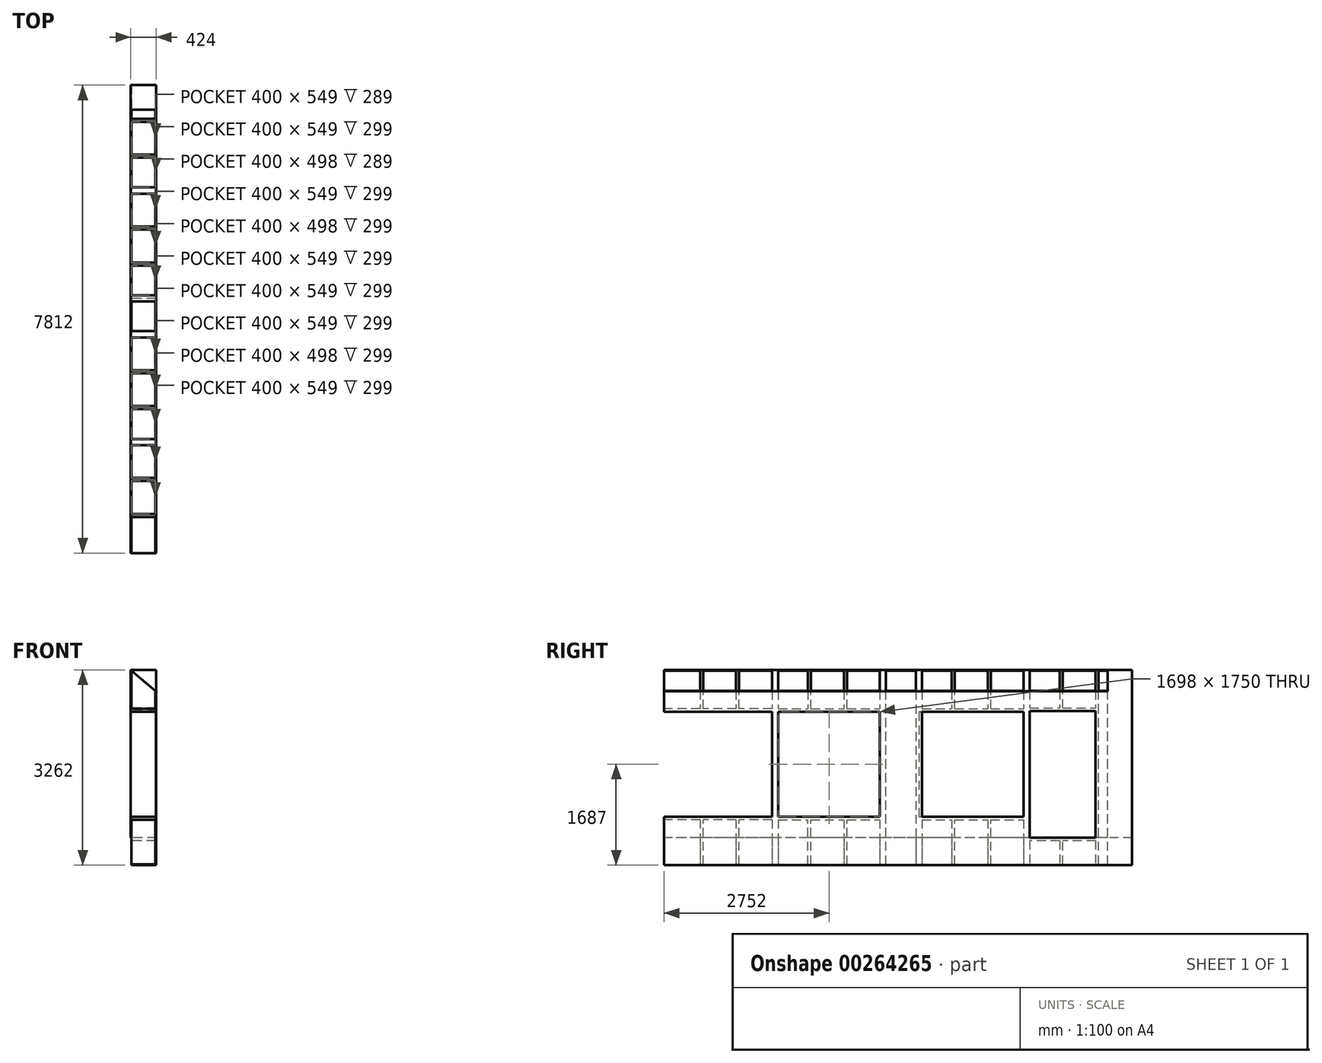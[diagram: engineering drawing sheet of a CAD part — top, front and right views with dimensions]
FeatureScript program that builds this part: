
annotation { "Feature Type Name" : "Feature", "Feature Type Description" : "" }
export const myFeature = defineFeature(function(context is Context, id is Id, definition is map)
    precondition{}
    {
        {
            var Q0;
            Q0=qCreatedBy(makeId("Right.planeOp"),FACE);
            var sketch = newSketch(context, id + "F0", { "sketchPlane" : qUnion([Q0])});
            skLineSegment(sketch, "E0.bottom", {"start": v(0, 0) * mm, "end": v(7400, 0) * mm});
            skLineSegment(sketch, "E0.top", {"start": v(0, 3250) * mm, "end": v(7400, 3250) * mm});
            skLineSegment(sketch, "E0.left", {"start": v(0, 0) * mm, "end": v(0, 3250) * mm});
            skLineSegment(sketch, "E0.right", {"start": v(7400, 0) * mm, "end": v(7400, 3250) * mm});
            skLineSegment(sketch, "E1", {"start": v(601, 3250) * mm, "end": v(601, 2601) * mm});
            skLineSegment(sketch, "E2", {"start": v(652, 0) * mm, "end": v(652, 749) * mm});
            skLineSegment(sketch, "E3.1.0.0", {"start": v(1252, 0) * mm, "end": v(1252, 749) * mm});
            skLineSegment(sketch, "E3.1.0.1", {"start": v(1201, 3250) * mm, "end": v(1201, 2601) * mm});
            skLineSegment(sketch, "E3.2.0.1", {"start": v(1801, 3250) * mm, "end": v(1801, 749) * mm});
            skLineSegment(sketch, "E3.4.0.0", {"start": v(3052, 0) * mm, "end": v(3052, 749) * mm});
            skLineSegment(sketch, "E3.4.0.1", {"start": v(3001, 3250) * mm, "end": v(3001, 2601) * mm});
            skLineSegment(sketch, "E3.5.0.1", {"start": v(3601, 3250) * mm, "end": v(3601, 0) * mm});
            skLineSegment(sketch, "E3.6.0.0", {"start": v(4252, 0) * mm, "end": v(4252, 3250) * mm});
            skLineSegment(sketch, "E3.6.0.1", {"start": v(4201, 3250) * mm, "end": v(4201, 0) * mm});
            skLineSegment(sketch, "E3.7.0.0", {"start": v(4852, 0) * mm, "end": v(4852, 749) * mm});
            skLineSegment(sketch, "E3.7.0.1", {"start": v(4801, 3250) * mm, "end": v(4801, 2601) * mm});
            skLineSegment(sketch, "E3.8.0.0", {"start": v(5452, 0) * mm, "end": v(5452, 749) * mm});
            skLineSegment(sketch, "E3.8.0.1", {"start": v(5401, 3250) * mm, "end": v(5401, 2601) * mm});
            skLineSegment(sketch, "E3.9.0.0", {"start": v(6052, 0) * mm, "end": v(6052, 749) * mm});
            skLineSegment(sketch, "E3.9.0.1", {"start": v(6001, 3250) * mm, "end": v(6001, 2601) * mm});
            skLineSegment(sketch, "E3.10.0.0", {"start": v(6652, 0) * mm, "end": v(6652, 399) * mm});
            skLineSegment(sketch, "E3.10.0.1", {"start": v(6601, 3250) * mm, "end": v(6601, 2611) * mm});
            skLineSegment(sketch, "E3.11.0.0", {"start": v(7252, 0) * mm, "end": v(7252, 3250) * mm});
            skLineSegment(sketch, "E3.11.0.1", {"start": v(7201, 3250) * mm, "end": v(7201, 0) * mm});
            skLineSegment(sketch, "E3.direction1", {"start": v(652, 0) * mm, "end": v(1252, 0) * mm, "construction": true});
            skLineSegment(sketch, "E4.bottom", {"start": v(7400, 0) * mm, "end": v(7812, 0) * mm});
            skLineSegment(sketch, "E4.top", {"start": v(7400, 3250) * mm, "end": v(7812, 3250) * mm});
            skLineSegment(sketch, "E4.right", {"start": v(7812, 0) * mm, "end": v(7812, 3250) * mm});
            skLineSegment(sketch, "E5", {"start": v(6001, 2550) * mm, "end": v(4252, 2550) * mm});
            skLineSegment(sketch, "E6", {"start": v(4252, 2550) * mm, "end": v(4252, 800) * mm});
            skLineSegment(sketch, "E7", {"start": v(4252, 800) * mm, "end": v(6001, 800) * mm});
            skLineSegment(sketch, "E8", {"start": v(4252, 2601) * mm, "end": v(6001, 2601) * mm});
            skLineSegment(sketch, "E9", {"start": v(4252, 749) * mm, "end": v(6001, 749) * mm});
            skLineSegment(sketch, "E10.trimOffspring", {"start": v(6001, 749) * mm, "end": v(6001, 0) * mm});
            skLineSegment(sketch, "E11.trimOffspring", {"start": v(6052, 2601) * mm, "end": v(6052, 3250) * mm});
            skLineSegment(sketch, "E12.trimOffspring", {"start": v(6601, 399) * mm, "end": v(6601, 0) * mm});
            skLineSegment(sketch, "E13.trimOffspring", {"start": v(6652, 2611) * mm, "end": v(6652, 3250) * mm});
            skLineSegment(sketch, "E14", {"start": v(0, 2550) * mm, "end": v(1801, 2550) * mm});
            skLineSegment(sketch, "E15", {"start": v(1801, 2601) * mm, "end": v(0, 2601) * mm});
            skLineSegment(sketch, "E16", {"start": v(1801, 749) * mm, "end": v(0, 749) * mm});
            skLineSegment(sketch, "E17", {"start": v(1801, 800) * mm, "end": v(0, 800) * mm});
            skLineSegment(sketch, "E18.trimOffspring", {"start": v(1201, 749) * mm, "end": v(1201, 0) * mm});
            skLineSegment(sketch, "E19.trimOffspring", {"start": v(1252, 2601) * mm, "end": v(1252, 3250) * mm});
            skLineSegment(sketch, "E20.trimOffspring", {"start": v(1801, 749) * mm, "end": v(1801, 0) * mm});
            skLineSegment(sketch, "E21.trimOffspring", {"start": v(3001, 749) * mm, "end": v(3001, 0) * mm});
            skLineSegment(sketch, "E22.trimOffspring", {"start": v(3052, 2601) * mm, "end": v(3052, 3250) * mm});
            skPoint(sketch, "E23.orphan", {"position": v(2401, 3250) * mm});
            skPoint(sketch, "E24.orphan", {"position": v(2401, 0) * mm});
            skLineSegment(sketch, "E25.trimOffspring", {"start": v(601, 749) * mm, "end": v(601, 0) * mm});
            skLineSegment(sketch, "E26.trimOffspring", {"start": v(652, 2601) * mm, "end": v(652, 3250) * mm});
            skLineSegment(sketch, "E27", {"start": v(1852, 3250) * mm, "end": v(1852, 0) * mm});
            skLineSegment(sketch, "E28", {"start": v(1903, 3250) * mm, "end": v(1903, 0) * mm});
            skLineSegment(sketch, "E29", {"start": v(1903, 2601) * mm, "end": v(3601, 2601) * mm});
            skLineSegment(sketch, "E30", {"start": v(1903, 2550) * mm, "end": v(3601, 2550) * mm});
            skLineSegment(sketch, "E31", {"start": v(3652, 3250) * mm, "end": v(3652, 0) * mm});
            skLineSegment(sketch, "E32", {"start": v(1903, 800) * mm, "end": v(3601, 800) * mm});
            skLineSegment(sketch, "E33", {"start": v(1903, 749) * mm, "end": v(3601, 749) * mm});
            skLineSegment(sketch, "E34", {"start": v(2401, 3250) * mm, "end": v(2401, 2601) * mm});
            skLineSegment(sketch, "E35", {"start": v(2401, 0) * mm, "end": v(2401, 749) * mm});
            skLineSegment(sketch, "E36", {"start": v(2452, 0) * mm, "end": v(2452, 749) * mm});
            skLineSegment(sketch, "E37", {"start": v(2452, 2601) * mm, "end": v(2452, 3250) * mm});
            skLineSegment(sketch, "E38", {"start": v(6052, 2601) * mm, "end": v(6052, 749) * mm});
            skLineSegment(sketch, "E39", {"start": v(6001, 2601) * mm, "end": v(6001, 749) * mm});
            skLineSegment(sketch, "E40", {"start": v(6103, 450) * mm, "end": v(7201, 450) * mm});
            skLineSegment(sketch, "E41", {"start": v(7201, 399) * mm, "end": v(6103, 399) * mm});
            skLineSegment(sketch, "E42", {"start": v(6103, 2560) * mm, "end": v(7201, 2560) * mm});
            skLineSegment(sketch, "E43", {"start": v(6103, 2611) * mm, "end": v(7201, 2611) * mm});
            skLineSegment(sketch, "E44", {"start": v(6103, 3250) * mm, "end": v(6103, 0) * mm});
            skLineSegment(sketch, "E45.trimOffspring", {"start": v(4801, 749) * mm, "end": v(4801, 0) * mm});
            skLineSegment(sketch, "E46.trimOffspring", {"start": v(4852, 2601) * mm, "end": v(4852, 3250) * mm});
            skLineSegment(sketch, "E47.trimOffspring", {"start": v(5401, 749) * mm, "end": v(5401, 0) * mm});
            skLineSegment(sketch, "E48.trimOffspring", {"start": v(5452, 2601) * mm, "end": v(5452, 3250) * mm});
            skPoint(sketch, "E49.orphan", {"position": v(6601, 2560) * mm});
            skPoint(sketch, "E50.orphan", {"position": v(6652, 2560) * mm});
            skPoint(sketch, "E51.orphan", {"position": v(6601, 450) * mm});
            skPoint(sketch, "E52.orphan", {"position": v(6652, 450) * mm});
            skLineSegment(sketch, "E53", {"start": v(4303, 3250) * mm, "end": v(4303, 0) * mm});
            skLineSegment(sketch, "E54", {"start": v(3703, 0) * mm, "end": v(3703, 3250) * mm});
            skSolve(sketch);
        }
        {
            var Q0;
            {var subQ0=sQuery(id+"F0.wireOp",EDGE,"E1");Q0=makeQuery(id+"F0.imprint","IMPRINT",FACE,{"disambiguationData":[TD([[makeQuery(id+"F0.imprint","IMPRINT",EDGE,{"derivedFrom":subQ0}),1.0]])]});}
            var Q1;
            {var subQ0=sQuery(id+"F0.wireOp",EDGE,"E3.7.0.0");Q1=makeQuery(id+"F0.imprint","IMPRINT",FACE,{"disambiguationData":[TD([[makeQuery(id+"F0.imprint","IMPRINT",EDGE,{"derivedFrom":subQ0}),1.0]])]});}
            var Q2;
            {var subQ0=sQuery(id+"F0.wireOp",EDGE,"E3.1.0.0");Q2=makeQuery(id+"F0.imprint","IMPRINT",FACE,{"disambiguationData":[TD([[makeQuery(id+"F0.imprint","IMPRINT",EDGE,{"derivedFrom":subQ0}),1.0]])]});}
            var Q3;
            {var subQ0=sQuery(id+"F0.wireOp",EDGE,"E3.2.0.0");Q3=makeQuery(id+"F0.imprint","IMPRINT",FACE,{"disambiguationData":[TD([[makeQuery(id+"F0.imprint","IMPRINT",EDGE,{"derivedFrom":subQ0}),1.0]])]});}
            var Q4;
            {var subQ0=sQuery(id+"F0.wireOp",EDGE,"E3.4.0.0");Q4=makeQuery(id+"F0.imprint","IMPRINT",FACE,{"disambiguationData":[TD([[makeQuery(id+"F0.imprint","IMPRINT",EDGE,{"derivedFrom":subQ0}),1.0]])]});}
            var Q5;
            {var subQ0=sQuery(id+"F0.wireOp",EDGE,"E3.5.0.0");Q5=makeQuery(id+"F0.imprint","IMPRINT",FACE,{"disambiguationData":[TD([[makeQuery(id+"F0.imprint","IMPRINT",EDGE,{"derivedFrom":subQ0}),1.0]])]});}
            var Q6;
            {var subQ0=sQuery(id+"F0.wireOp",EDGE,"E3.9.0.0");Q6=makeQuery(id+"F0.imprint","IMPRINT",FACE,{"disambiguationData":[TD([[makeQuery(id+"F0.imprint","IMPRINT",EDGE,{"derivedFrom":subQ0}),1.0]])]});}
            var Q7;
            {var subQ0=sQuery(id+"F0.wireOp",EDGE,"E3.10.0.0");Q7=makeQuery(id+"F0.imprint","IMPRINT",FACE,{"disambiguationData":[TD([[makeQuery(id+"F0.imprint","IMPRINT",EDGE,{"derivedFrom":subQ0}),1.0]])]});}
            var Q8;
            {var subQ0=sQuery(id+"F0.wireOp",EDGE,"E3.1.0.1");Q8=makeQuery(id+"F0.imprint","IMPRINT",FACE,{"disambiguationData":[TD([[makeQuery(id+"F0.imprint","IMPRINT",EDGE,{"derivedFrom":subQ0}),1.0]])]});}
            var Q9;
            {var subQ0=sQuery(id+"F0.wireOp",EDGE,"E3.2.0.1");Q9=makeQuery(id+"F0.imprint","IMPRINT",FACE,{"disambiguationData":[TD([[makeQuery(id+"F0.imprint","IMPRINT",EDGE,{"derivedFrom":subQ0}),1.0]])]});}
            var Q10;
            {var subQ0=sQuery(id+"F0.wireOp",EDGE,"E3.4.0.1");Q10=makeQuery(id+"F0.imprint","IMPRINT",FACE,{"disambiguationData":[TD([[makeQuery(id+"F0.imprint","IMPRINT",EDGE,{"derivedFrom":subQ0}),1.0]])]});}
            var Q11;
            {var subQ0=sQuery(id+"F0.wireOp",EDGE,"E3.5.0.1");Q11=makeQuery(id+"F0.imprint","IMPRINT",FACE,{"disambiguationData":[TD([[makeQuery(id+"F0.imprint","IMPRINT",EDGE,{"derivedFrom":subQ0}),1.0]])]});}
            var Q12;
            {var subQ0=sQuery(id+"F0.wireOp",EDGE,"E3.9.0.1");Q12=makeQuery(id+"F0.imprint","IMPRINT",FACE,{"disambiguationData":[TD([[makeQuery(id+"F0.imprint","IMPRINT",EDGE,{"derivedFrom":subQ0}),1.0]])]});}
            var Q13;
            {var subQ0=sQuery(id+"F0.wireOp",EDGE,"E3.10.0.1");Q13=makeQuery(id+"F0.imprint","IMPRINT",FACE,{"disambiguationData":[TD([[makeQuery(id+"F0.imprint","IMPRINT",EDGE,{"derivedFrom":subQ0}),1.0]])]});}
            var Q14;
            {var subQ4=sQuery(id+"F0.wireOp",EDGE,"E3.3.0.0");Q14=makeQuery(id+"F0.imprint","IMPRINT",FACE,{"disambiguationData":[TD([[makeQuery(id+"F0.imprint","IMPRINT",EDGE,{"derivedFrom":subQ4}),1.0]])]});}
            var Q15;
            {var subQ4=sQuery(id+"F0.wireOp",EDGE,"E3.3.0.0");Q15=makeQuery(id+"F0.imprint","IMPRINT",FACE,{"disambiguationData":[TD([[makeQuery(id+"F0.imprint","IMPRINT",EDGE,{"derivedFrom":subQ4}),-1.0]])]});}
            var Q16;
            {var subQ0=sQuery(id+"F0.wireOp",EDGE,"E3.6.0.0");Q16=makeQuery(id+"F0.imprint","IMPRINT",FACE,{"disambiguationData":[TD([[makeQuery(id+"F0.imprint","IMPRINT",EDGE,{"derivedFrom":subQ0}),1.0]])]});}
            var Q17;
            {var subQ5=sQuery(id+"F0.wireOp",EDGE,"E3.8.0.1");Q17=makeQuery(id+"F0.imprint","IMPRINT",FACE,{"disambiguationData":[TD([[makeQuery(id+"F0.imprint","IMPRINT",EDGE,{"derivedFrom":subQ5}),1.0]])]});}
            var Q18;
            {var subQ4=sQuery(id+"F0.wireOp",EDGE,"E3.11.0.0");Q18=makeQuery(id+"F0.imprint","IMPRINT",FACE,{"disambiguationData":[TD([[makeQuery(id+"F0.imprint","IMPRINT",EDGE,{"derivedFrom":subQ4}),1.0]])]});}
            var Q19;
            {var subQ6=sQuery(id+"F0.wireOp",EDGE,"E17");Q19=makeQuery(id+"F0.imprint","IMPRINT",FACE,{"disambiguationData":[TD([[makeQuery(id+"F0.imprint","IMPRINT",EDGE,{"derivedFrom":subQ6}),1.0]])]});}
            var Q20;
            {var subQ5=sQuery(id+"F0.wireOp",EDGE,"E14");Q20=makeQuery(id+"F0.imprint","IMPRINT",FACE,{"disambiguationData":[TD([[makeQuery(id+"F0.imprint","IMPRINT",EDGE,{"derivedFrom":subQ5}),1.0]])]});}
            var Q21;
            {var subQ5=sQuery(id+"F0.wireOp",EDGE,"g8gJmtVJ-kyqd-3TZ6-0mUu-25J443NQGefS");Q21=makeQuery(id+"F0.imprint","IMPRINT",FACE,{"disambiguationData":[TD([[makeQuery(id+"F0.imprint","IMPRINT",EDGE,{"derivedFrom":subQ5}),1.0]])]});}
            var Q22;
            {var subQ4=sQuery(id+"F0.wireOp",EDGE,"8giRP16X-JChZ-mFzo-qgzl-EssFRHRw9BJs");Q22=makeQuery(id+"F0.imprint","IMPRINT",FACE,{"disambiguationData":[TD([[makeQuery(id+"F0.imprint","IMPRINT",EDGE,{"derivedFrom":subQ4}),-1.0]])]});}
            var Q23;
            Q23=makeQuery(id+"F0.imprint","IMPRINT",FACE,{"disambiguationData":[TD([[makeQuery(id+"F0.imprint","IMPRINT",EDGE,{"derivedFrom":sQuery(id+"F0.wireOp",EDGE,"E4.bottom")}),1.0]])]});
            var Q24;
            {var subQ4=sQuery(id+"F0.wireOp",EDGE,"E7");Q24=makeQuery(id+"F0.imprint","IMPRINT",FACE,{"disambiguationData":[TD([[makeQuery(id+"F0.imprint","IMPRINT",EDGE,{"derivedFrom":subQ4}),-1.0]])]});}
            var Q25;
            {var subQ0=sQuery(id+"F0.wireOp",EDGE,"E2");Q25=makeQuery(id+"F0.imprint","IMPRINT",FACE,{"disambiguationData":[TD([[makeQuery(id+"F0.imprint","IMPRINT",EDGE,{"derivedFrom":subQ0}),1.0]])]});}
            var Q26;
            {var subQ4=sQuery(id+"F0.wireOp",EDGE,"E27");Q26=makeQuery(id+"F0.imprint","IMPRINT",FACE,{"disambiguationData":[TD([[makeQuery(id+"F0.imprint","IMPRINT",EDGE,{"derivedFrom":subQ4}),1.0]])]});}
            var Q27;
            {var subQ0=sQuery(id+"F0.wireOp",EDGE,"E32");Q27=makeQuery(id+"F0.imprint","IMPRINT",FACE,{"disambiguationData":[TD([[makeQuery(id+"F0.imprint","IMPRINT",EDGE,{"derivedFrom":subQ0}),-1.0]])]});}
            var Q28;
            {var subQ0=sQuery(id+"F0.wireOp",EDGE,"E35");Q28=makeQuery(id+"F0.imprint","IMPRINT",FACE,{"disambiguationData":[TD([[makeQuery(id+"F0.imprint","IMPRINT",EDGE,{"derivedFrom":subQ0}),-1.0]])]});}
            var Q29;
            {var subQ0=sQuery(id+"F0.wireOp",EDGE,"E34");Q29=makeQuery(id+"F0.imprint","IMPRINT",FACE,{"disambiguationData":[TD([[makeQuery(id+"F0.imprint","IMPRINT",EDGE,{"derivedFrom":subQ0}),1.0]])]});}
            var Q30;
            {var subQ5=sQuery(id+"F0.wireOp",EDGE,"E30");Q30=makeQuery(id+"F0.imprint","IMPRINT",FACE,{"disambiguationData":[TD([[makeQuery(id+"F0.imprint","IMPRINT",EDGE,{"derivedFrom":subQ5}),1.0]])]});}
            var Q31;
            {var subQ3=sQuery(id+"F0.wireOp",EDGE,"E42");Q31=makeQuery(id+"F0.imprint","IMPRINT",FACE,{"disambiguationData":[TD([[makeQuery(id+"F0.imprint","IMPRINT",EDGE,{"derivedFrom":subQ3}),1.0]])]});}
            var Q32;
            {var subQ3=sQuery(id+"F0.wireOp",EDGE,"E40");Q32=makeQuery(id+"F0.imprint","IMPRINT",FACE,{"disambiguationData":[TD([[makeQuery(id+"F0.imprint","IMPRINT",EDGE,{"derivedFrom":subQ3}),-1.0]])]});}
            var Q33;
            {var subQ0=sQuery(id+"F0.wireOp",EDGE,"E3.8.0.0");Q33=makeQuery(id+"F0.imprint","IMPRINT",FACE,{"disambiguationData":[TD([[makeQuery(id+"F0.imprint","IMPRINT",EDGE,{"derivedFrom":subQ0}),1.0]])]});}
            var Q34;
            {var subQ0=sQuery(id+"F0.wireOp",EDGE,"E3.9.0.0");Q34=makeQuery(id+"F0.imprint","IMPRINT",FACE,{"disambiguationData":[TD([[makeQuery(id+"F0.imprint","IMPRINT",EDGE,{"derivedFrom":subQ0}),-1.0]])]});}
            var Q35;
            {var subQ0=sQuery(id+"F0.wireOp",EDGE,"E3.7.0.1");Q35=makeQuery(id+"F0.imprint","IMPRINT",FACE,{"disambiguationData":[TD([[makeQuery(id+"F0.imprint","IMPRINT",EDGE,{"derivedFrom":subQ0}),1.0]])]});}
            var Q36;
            {var subQ4=sQuery(id+"F0.wireOp",EDGE,"E5");var subQ8=sQuery(id+"F0.wireOp",EDGE,"E39");var subQ9=makeQuery(id+"F0.imprint","INTERSECT",VERTEX,{"derivedFrom":[subQ4,subQ8]});Q36=makeQuery(id+"F0.imprint","IMPRINT",FACE,{"disambiguationData":[TD([[makeQuery(id+"F0.imprint","IMPRINT",EDGE,{"disambiguationData":[TD([[subQ9,-1.0]])],"derivedFrom":subQ4}),-1.0]])]});}
            var Q37;
            {var subQ0=sQuery(id+"F0.wireOp",EDGE,"E3.6.0.0");var subQ1=sQuery(id+"F0.wireOp",EDGE,"E0.top");var subQ2=makeQuery(id+"F0.imprint","INTERSECT",VERTEX,{"derivedFrom":[subQ1,subQ0]});Q37=makeQuery(id+"F0.imprint","IMPRINT",FACE,{"disambiguationData":[TD([[makeQuery(id+"F0.imprint","IMPRINT",EDGE,{"disambiguationData":[TD([[subQ2,-1.0]])],"derivedFrom":subQ1}),-1.0]])]});}
            var Q38;
            {var subQ0=sQuery(id+"F0.wireOp",EDGE,"E6");Q38=makeQuery(id+"F0.imprint","IMPRINT",FACE,{"disambiguationData":[TD([[makeQuery(id+"F0.imprint","IMPRINT",EDGE,{"derivedFrom":subQ0}),1.0]])]});}
            var Q39;
            {var subQ1=sQuery(id+"F0.wireOp",EDGE,"E3.6.0.0");var subQ3=sQuery(id+"F0.wireOp",EDGE,"E8");var subQ4=makeQuery(id+"F0.imprint","INTERSECT",VERTEX,{"derivedFrom":[subQ1,subQ3]});Q39=makeQuery(id+"F0.imprint","IMPRINT",FACE,{"disambiguationData":[TD([[makeQuery(id+"F0.imprint","IMPRINT",EDGE,{"disambiguationData":[TD([[subQ4,-1.0]])],"derivedFrom":subQ3}),-1.0]])]});}
            var Q40;
            {var subQ6=sQuery(id+"F0.wireOp",EDGE,"E39");var subQ7=sQuery(id+"F0.wireOp",EDGE,"E7");var subQ8=makeQuery(id+"F0.imprint","INTERSECT",VERTEX,{"derivedFrom":[subQ7,subQ6]});Q40=makeQuery(id+"F0.imprint","IMPRINT",FACE,{"disambiguationData":[TD([[makeQuery(id+"F0.imprint","IMPRINT",EDGE,{"disambiguationData":[TD([[subQ8,1.0]])],"derivedFrom":subQ7}),-1.0]])]});}
            var Q41;
            {var subQ0=sQuery(id+"F0.wireOp",EDGE,"E3.6.0.0");var subQ1=sQuery(id+"F0.wireOp",EDGE,"E0.bottom");var subQ2=makeQuery(id+"F0.imprint","INTERSECT",VERTEX,{"derivedFrom":[subQ1,subQ0]});Q41=makeQuery(id+"F0.imprint","IMPRINT",FACE,{"disambiguationData":[TD([[makeQuery(id+"F0.imprint","IMPRINT",EDGE,{"disambiguationData":[TD([[subQ2,-1.0]])],"derivedFrom":subQ1}),1.0]])]});}
            var Q42;
            {var subQ0=sQuery(id+"F0.wireOp",EDGE,"E31");Q42=makeQuery(id+"F0.imprint","IMPRINT",FACE,{"disambiguationData":[TD([[makeQuery(id+"F0.imprint","IMPRINT",EDGE,{"derivedFrom":subQ0}),1.0]])]});}
            extrude(context, id + "F1", {"entities" : qUnion([Q0, Q1, Q2, Q3, Q4, Q5, Q6, Q7, Q8, Q9, Q10, Q11, Q12, Q13, Q14, Q15, Q16, Q17, Q18, Q19, Q20, Q21, Q22, Q23, Q24, Q25, Q26, Q27, Q28, Q29, Q30, Q31, Q32, Q33, Q34, Q35, Q36, Q37, Q38, Q39, Q40, Q41, Q42]), "depth" : 400 * mm, "offsetDistance" : 25 * mm});
        }
        {
            var Q0;
            Q0=makeQuery(id+"F1.opExtrude","CAP_FACE",FACE,{"disambiguationData":[OSD([sQuery(id+"F0.wireOp",EDGE,"E0.bottom"),sQuery(id+"F0.wireOp",EDGE,"E0.top"),sQuery(id+"F0.wireOp",EDGE,"E1"),sQuery(id+"F0.wireOp",EDGE,"E3.1.0.0"),sQuery(id+"F0.wireOp",EDGE,"E3.1.0.1"),sQuery(id+"F0.wireOp",EDGE,"E3.2.0.0"),sQuery(id+"F0.wireOp",EDGE,"E3.2.0.1"),sQuery(id+"F0.wireOp",EDGE,"E3.3.0.1"),sQuery(id+"F0.wireOp",EDGE,"E3.4.0.0"),sQuery(id+"F0.wireOp",EDGE,"E3.4.0.1"),sQuery(id+"F0.wireOp",EDGE,"E3.5.0.0"),sQuery(id+"F0.wireOp",EDGE,"E3.5.0.1"),sQuery(id+"F0.wireOp",EDGE,"E3.6.0.0"),sQuery(id+"F0.wireOp",EDGE,"E3.6.0.1"),sQuery(id+"F0.wireOp",EDGE,"E14"),sQuery(id+"F0.wireOp",EDGE,"E15"),sQuery(id+"F0.wireOp",EDGE,"E16"),sQuery(id+"F0.wireOp",EDGE,"E17"),sQuery(id+"F0.wireOp",EDGE,"E18.trimOffspring"),sQuery(id+"F0.wireOp",EDGE,"E19.trimOffspring"),sQuery(id+"F0.wireOp",EDGE,"E20.trimOffspring"),sQuery(id+"F0.wireOp",EDGE,"9c03632e-1589-4136-8b4a-7c2474c811de.trimOffspring"),sQuery(id+"F0.wireOp",EDGE,"q5mhnWq2-EtEE-7vjZ-CXv9-tcfamw4Ga4Gx"),sQuery(id+"F0.wireOp",EDGE,"FWBOiuXw-SkXY-gYsp-Law7-7kdNVkWK1UfF"),sQuery(id+"F0.wireOp",EDGE,"g8gJmtVJ-kyqd-3TZ6-0mUu-25J443NQGefS"),sQuery(id+"F0.wireOp",EDGE,"8giRP16X-JChZ-mFzo-qgzl-EssFRHRw9BJs"),sQuery(id+"F0.wireOp",EDGE,"Jl1Ox0xb-Z49W-AvNk-nDFi-4VLoJo9j3xGR"),sQuery(id+"F0.wireOp",EDGE,"E21.trimOffspring"),sQuery(id+"F0.wireOp",EDGE,"E22.trimOffspring"),sQuery(id+"F0.wireOp",EDGE,"a5652450-98d4-451b-b7c5-3669fa653a12.trimOffspring"),sQuery(id+"F0.wireOp",EDGE,"9c86828a-2c14-4f8d-8b37-fce8d1982b22.trimOffspring"),sQuery(id+"F0.wireOp",EDGE,"YK2BJbLm-Syb8-vEb6-AO3p-bAR0vb5wNjTQ")])],"isStart":false});
            var sketch = newSketch(context, id + "F2", { "sketchPlane" : qUnion([Q0])});
            skLineSegment(sketch, "E55.bottom", {"start": v(0, 0) * mm, "end": v(7812, 0) * mm});
            skLineSegment(sketch, "E55.top", {"start": v(0, 3250) * mm, "end": v(7812, 3250) * mm});
            skLineSegment(sketch, "E55.left", {"start": v(0, 0) * mm, "end": v(0, 3250) * mm});
            skLineSegment(sketch, "E56.bottom", {"start": v(0, 2550) * mm, "end": v(1801, 2550) * mm});
            skLineSegment(sketch, "E56.top", {"start": v(0, 800) * mm, "end": v(1801, 800) * mm});
            skLineSegment(sketch, "E56.left", {"start": v(0, 2550) * mm, "end": v(0, 800) * mm});
            skLineSegment(sketch, "E56.right", {"start": v(1801, 2550) * mm, "end": v(1801, 800) * mm});
            skLineSegment(sketch, "E57.bottom", {"start": v(1903, 800) * mm, "end": v(3601, 800) * mm});
            skLineSegment(sketch, "E57.top", {"start": v(1903, 2550) * mm, "end": v(3601, 2550) * mm});
            skLineSegment(sketch, "E57.left", {"start": v(1903, 2550) * mm, "end": v(1903, 800) * mm});
            skLineSegment(sketch, "E57.right", {"start": v(3601, 2550) * mm, "end": v(3601, 800) * mm});
            skLineSegment(sketch, "E58", {"start": v(7812, 0) * mm, "end": v(7812, 3250) * mm});
            skLineSegment(sketch, "E59.bottom", {"start": v(4303, 2550) * mm, "end": v(6001, 2550) * mm});
            skLineSegment(sketch, "E59.top", {"start": v(4303, 800) * mm, "end": v(6001, 800) * mm});
            skLineSegment(sketch, "E59.left", {"start": v(4303, 2550) * mm, "end": v(4303, 800) * mm});
            skLineSegment(sketch, "E59.right", {"start": v(6001, 2550) * mm, "end": v(6001, 800) * mm});
            skLineSegment(sketch, "E60.bottom", {"start": v(6103, 2560) * mm, "end": v(7201, 2560) * mm});
            skLineSegment(sketch, "E60.top", {"start": v(6103, 450) * mm, "end": v(7201, 450) * mm});
            skLineSegment(sketch, "E60.left", {"start": v(6103, 2560) * mm, "end": v(6103, 450) * mm});
            skLineSegment(sketch, "E60.right", {"start": v(7201, 2560) * mm, "end": v(7201, 450) * mm});
            skSolve(sketch);
        }
        {
            var Q0;
            {var subQ1=sQuery(id+"F0.wireOp",EDGE,"E25.trimOffspring");var subQ2=makeQuery(id+"F1.opExtrude","CAP_EDGE",EDGE,{"disambiguationData":[OSD([subQ1])],"isStart":false});Q0=makeQuery(id+"F2.imprint","IMPRINT",FACE,{"disambiguationData":[TD([[makeQuery(id+"F2.imprint","IMPRINT",EDGE,{"derivedFrom":subQ2}),-1.0]])]});}
            var Q1;
            {var subQ1=sQuery(id+"F0.wireOp",EDGE,"E2");var subQ2=makeQuery(id+"F1.opExtrude","CAP_EDGE",EDGE,{"disambiguationData":[OSD([subQ1])],"isStart":false});Q1=makeQuery(id+"F2.imprint","IMPRINT",FACE,{"disambiguationData":[TD([[makeQuery(id+"F2.imprint","IMPRINT",EDGE,{"derivedFrom":subQ2}),-1.0]])]});}
            var Q2;
            {var subQ1=sQuery(id+"F0.wireOp",EDGE,"E3.1.0.0");var subQ2=makeQuery(id+"F1.opExtrude","CAP_EDGE",EDGE,{"disambiguationData":[OSD([subQ1])],"isStart":false});Q2=makeQuery(id+"F2.imprint","IMPRINT",FACE,{"disambiguationData":[TD([[makeQuery(id+"F2.imprint","IMPRINT",EDGE,{"derivedFrom":subQ2}),-1.0]])]});}
            var Q3;
            {var subQ5=sQuery(id+"F0.wireOp",EDGE,"E35");var subQ6=makeQuery(id+"F1.opExtrude","CAP_EDGE",EDGE,{"disambiguationData":[OSD([subQ5])],"isStart":false});Q3=makeQuery(id+"F2.imprint","IMPRINT",FACE,{"disambiguationData":[TD([[makeQuery(id+"F2.imprint","IMPRINT",EDGE,{"derivedFrom":subQ6}),1.0]])]});}
            var Q4;
            {var subQ1=sQuery(id+"F0.wireOp",EDGE,"E21.trimOffspring");var subQ2=makeQuery(id+"F1.opExtrude","CAP_EDGE",EDGE,{"disambiguationData":[OSD([subQ1])],"isStart":false});Q4=makeQuery(id+"F2.imprint","IMPRINT",FACE,{"disambiguationData":[TD([[makeQuery(id+"F2.imprint","IMPRINT",EDGE,{"derivedFrom":subQ2}),-1.0]])]});}
            var Q5;
            {var subQ1=sQuery(id+"F0.wireOp",EDGE,"E3.4.0.0");var subQ2=makeQuery(id+"F1.opExtrude","CAP_EDGE",EDGE,{"disambiguationData":[OSD([subQ1])],"isStart":false});Q5=makeQuery(id+"F2.imprint","IMPRINT",FACE,{"disambiguationData":[TD([[makeQuery(id+"F2.imprint","IMPRINT",EDGE,{"derivedFrom":subQ2}),-1.0]])]});}
            var Q6;
            {var subQ1=sQuery(id+"F0.wireOp",EDGE,"E1");var subQ2=makeQuery(id+"F1.opExtrude","CAP_EDGE",EDGE,{"disambiguationData":[OSD([subQ1])],"isStart":false});Q6=makeQuery(id+"F2.imprint","IMPRINT",FACE,{"disambiguationData":[TD([[makeQuery(id+"F2.imprint","IMPRINT",EDGE,{"derivedFrom":subQ2}),-1.0]])]});}
            var Q7;
            {var subQ1=sQuery(id+"F0.wireOp",EDGE,"E3.1.0.1");var subQ2=makeQuery(id+"F1.opExtrude","CAP_EDGE",EDGE,{"disambiguationData":[OSD([subQ1])],"isStart":false});Q7=makeQuery(id+"F2.imprint","IMPRINT",FACE,{"disambiguationData":[TD([[makeQuery(id+"F2.imprint","IMPRINT",EDGE,{"derivedFrom":subQ2}),-1.0]])]});}
            var Q8;
            {var subQ5=sQuery(id+"F0.wireOp",EDGE,"E19.trimOffspring");var subQ6=makeQuery(id+"F1.opExtrude","CAP_EDGE",EDGE,{"disambiguationData":[OSD([subQ5])],"isStart":false});Q8=makeQuery(id+"F2.imprint","IMPRINT",FACE,{"disambiguationData":[TD([[makeQuery(id+"F2.imprint","IMPRINT",EDGE,{"derivedFrom":subQ6}),-1.0]])]});}
            var Q9;
            {var subQ5=sQuery(id+"F0.wireOp",EDGE,"E34");var subQ6=makeQuery(id+"F1.opExtrude","CAP_EDGE",EDGE,{"disambiguationData":[OSD([subQ5])],"isStart":false});Q9=makeQuery(id+"F2.imprint","IMPRINT",FACE,{"disambiguationData":[TD([[makeQuery(id+"F2.imprint","IMPRINT",EDGE,{"derivedFrom":subQ6}),-1.0]])]});}
            var Q10;
            {var subQ1=sQuery(id+"F0.wireOp",EDGE,"E3.4.0.1");var subQ2=makeQuery(id+"F1.opExtrude","CAP_EDGE",EDGE,{"disambiguationData":[OSD([subQ1])],"isStart":false});Q10=makeQuery(id+"F2.imprint","IMPRINT",FACE,{"disambiguationData":[TD([[makeQuery(id+"F2.imprint","IMPRINT",EDGE,{"derivedFrom":subQ2}),-1.0]])]});}
            var Q11;
            {var subQ5=sQuery(id+"F0.wireOp",EDGE,"E22.trimOffspring");var subQ6=makeQuery(id+"F1.opExtrude","CAP_EDGE",EDGE,{"disambiguationData":[OSD([subQ5])],"isStart":false});Q11=makeQuery(id+"F2.imprint","IMPRINT",FACE,{"disambiguationData":[TD([[makeQuery(id+"F2.imprint","IMPRINT",EDGE,{"derivedFrom":subQ6}),-1.0]])]});}
            var Q12;
            Q12=makeQuery(id+"F2.imprint","IMPRINT",FACE,{"disambiguationData":[TD([[makeQuery(id+"F2.imprint","IMPRINT",EDGE,{"derivedFrom":sQuery(id+"F2.wireOp",EDGE,"i0whRvaI-gCvx-6G9T-CPu5-F9c6RNk1h4tm.bottom")}),1.0]])]});
            var Q13;
            {var subQ59=sQuery(id+"F2.wireOp",EDGE,"E56.bottom");Q13=makeQuery(id+"F2.imprint","IMPRINT",FACE,{"disambiguationData":[TD([[makeQuery(id+"F2.imprint","IMPRINT",EDGE,{"derivedFrom":subQ59}),1.0]])]});}
            var Q14;
            {var subQ2=sQuery(id+"F2.wireOp",EDGE,"E58");Q14=makeQuery(id+"F2.imprint","IMPRINT",FACE,{"disambiguationData":[TD([[makeQuery(id+"F2.imprint","IMPRINT",EDGE,{"derivedFrom":subQ2}),1.0]])]});}
            extrude(context, id + "F3", {"entities" : qUnion([Q0, Q1, Q2, Q3, Q4, Q5, Q6, Q7, Q8, Q9, Q10, Q11, Q12, Q13, Q14]), "operationType" : NewBodyOperationType.ADD, "depth" : 12 * mm, "offsetDistance" : 25 * mm});
        }
        {
            var Q0;
            Q0=makeQuery(id+"F1.opExtrude","CAP_FACE",FACE,{"disambiguationData":[OSD([sQuery(id+"F0.wireOp",EDGE,"E0.bottom"),sQuery(id+"F0.wireOp",EDGE,"E0.top"),sQuery(id+"F0.wireOp",EDGE,"E1"),sQuery(id+"F0.wireOp",EDGE,"E3.1.0.0"),sQuery(id+"F0.wireOp",EDGE,"E3.1.0.1"),sQuery(id+"F0.wireOp",EDGE,"E3.2.0.0"),sQuery(id+"F0.wireOp",EDGE,"E3.2.0.1"),sQuery(id+"F0.wireOp",EDGE,"E3.3.0.1"),sQuery(id+"F0.wireOp",EDGE,"E3.4.0.0"),sQuery(id+"F0.wireOp",EDGE,"E3.4.0.1"),sQuery(id+"F0.wireOp",EDGE,"E3.5.0.0"),sQuery(id+"F0.wireOp",EDGE,"E3.5.0.1"),sQuery(id+"F0.wireOp",EDGE,"E3.6.0.0"),sQuery(id+"F0.wireOp",EDGE,"E3.6.0.1"),sQuery(id+"F0.wireOp",EDGE,"E14"),sQuery(id+"F0.wireOp",EDGE,"E15"),sQuery(id+"F0.wireOp",EDGE,"E16"),sQuery(id+"F0.wireOp",EDGE,"E17"),sQuery(id+"F0.wireOp",EDGE,"E18.trimOffspring"),sQuery(id+"F0.wireOp",EDGE,"E19.trimOffspring"),sQuery(id+"F0.wireOp",EDGE,"E20.trimOffspring"),sQuery(id+"F0.wireOp",EDGE,"9c03632e-1589-4136-8b4a-7c2474c811de.trimOffspring"),sQuery(id+"F0.wireOp",EDGE,"q5mhnWq2-EtEE-7vjZ-CXv9-tcfamw4Ga4Gx"),sQuery(id+"F0.wireOp",EDGE,"FWBOiuXw-SkXY-gYsp-Law7-7kdNVkWK1UfF"),sQuery(id+"F0.wireOp",EDGE,"g8gJmtVJ-kyqd-3TZ6-0mUu-25J443NQGefS"),sQuery(id+"F0.wireOp",EDGE,"8giRP16X-JChZ-mFzo-qgzl-EssFRHRw9BJs"),sQuery(id+"F0.wireOp",EDGE,"Jl1Ox0xb-Z49W-AvNk-nDFi-4VLoJo9j3xGR"),sQuery(id+"F0.wireOp",EDGE,"E21.trimOffspring"),sQuery(id+"F0.wireOp",EDGE,"E22.trimOffspring"),sQuery(id+"F0.wireOp",EDGE,"a5652450-98d4-451b-b7c5-3669fa653a12.trimOffspring"),sQuery(id+"F0.wireOp",EDGE,"9c86828a-2c14-4f8d-8b37-fce8d1982b22.trimOffspring"),sQuery(id+"F0.wireOp",EDGE,"YK2BJbLm-Syb8-vEb6-AO3p-bAR0vb5wNjTQ")])],"isStart":true});
            var sketch = newSketch(context, id + "F4", { "sketchPlane" : qUnion([Q0])});
            skLineSegment(sketch, "E61.bottom", {"start": v(-3601, 2550) * mm, "end": v(-1903, 2550) * mm});
            skLineSegment(sketch, "E61.top", {"start": v(-3601, 800) * mm, "end": v(-1903, 800) * mm});
            skLineSegment(sketch, "E61.left", {"start": v(-3601, 2550) * mm, "end": v(-3601, 800) * mm});
            skLineSegment(sketch, "E61.right", {"start": v(-1903, 2550) * mm, "end": v(-1903, 800) * mm});
            skLineSegment(sketch, "E62.bottom", {"start": v(-1801, 2550) * mm, "end": v(0, 2550) * mm});
            skLineSegment(sketch, "E62.top", {"start": v(-1801, 800) * mm, "end": v(0, 800) * mm});
            skLineSegment(sketch, "E62.left", {"start": v(0, 2550) * mm, "end": v(0, 800) * mm});
            skLineSegment(sketch, "E62.right", {"start": v(-1801, 2550) * mm, "end": v(-1801, 800) * mm});
            skLineSegment(sketch, "E63.bottom", {"start": v(-7812, 3250) * mm, "end": v(0, 3250) * mm});
            skLineSegment(sketch, "E63.top", {"start": v(-7812, 450) * mm, "end": v(0, 450) * mm});
            skLineSegment(sketch, "E63.left", {"start": v(-7812, 3250) * mm, "end": v(-7812, 450) * mm});
            skLineSegment(sketch, "E63.right", {"start": v(0, 3250) * mm, "end": v(0, 450) * mm});
            skLineSegment(sketch, "E64.bottom", {"start": v(-4252, 2550) * mm, "end": v(-6001, 2550) * mm});
            skLineSegment(sketch, "E64.top", {"start": v(-4252, 800) * mm, "end": v(-6001, 800) * mm});
            skLineSegment(sketch, "E64.left", {"start": v(-4252, 2550) * mm, "end": v(-4252, 800) * mm});
            skLineSegment(sketch, "E64.right", {"start": v(-6001, 2550) * mm, "end": v(-6001, 800) * mm});
            skLineSegment(sketch, "E65.bottom", {"start": v(-7201, 2560) * mm, "end": v(-6103, 2560) * mm});
            skLineSegment(sketch, "E65.top", {"start": v(-7201, 450) * mm, "end": v(-6103, 450) * mm});
            skLineSegment(sketch, "E65.left", {"start": v(-7201, 2560) * mm, "end": v(-7201, 450) * mm});
            skLineSegment(sketch, "E65.right", {"start": v(-6103, 2560) * mm, "end": v(-6103, 450) * mm});
            skSolve(sketch);
        }
        {
            var Q0;
            {var subQ5=sQuery(id+"F0.wireOp",EDGE,"E22.trimOffspring");var subQ6=makeQuery(id+"F1.opExtrude","CAP_EDGE",EDGE,{"disambiguationData":[OSD([subQ5])],"isStart":true});Q0=makeQuery(id+"F4.imprint","IMPRINT",FACE,{"disambiguationData":[TD([[makeQuery(id+"F4.imprint","IMPRINT",EDGE,{"derivedFrom":subQ6}),1.0]])]});}
            var Q1;
            {var subQ1=sQuery(id+"F0.wireOp",EDGE,"E3.4.0.1");var subQ2=makeQuery(id+"F1.opExtrude","CAP_EDGE",EDGE,{"disambiguationData":[OSD([subQ1])],"isStart":true});Q1=makeQuery(id+"F4.imprint","IMPRINT",FACE,{"disambiguationData":[TD([[makeQuery(id+"F4.imprint","IMPRINT",EDGE,{"derivedFrom":subQ2}),1.0]])]});}
            var Q2;
            {var subQ5=sQuery(id+"F0.wireOp",EDGE,"E34");var subQ6=makeQuery(id+"F1.opExtrude","CAP_EDGE",EDGE,{"disambiguationData":[OSD([subQ5])],"isStart":true});Q2=makeQuery(id+"F4.imprint","IMPRINT",FACE,{"disambiguationData":[TD([[makeQuery(id+"F4.imprint","IMPRINT",EDGE,{"derivedFrom":subQ6}),1.0]])]});}
            var Q3;
            {var subQ5=sQuery(id+"F0.wireOp",EDGE,"E19.trimOffspring");var subQ6=makeQuery(id+"F1.opExtrude","CAP_EDGE",EDGE,{"disambiguationData":[OSD([subQ5])],"isStart":true});Q3=makeQuery(id+"F4.imprint","IMPRINT",FACE,{"disambiguationData":[TD([[makeQuery(id+"F4.imprint","IMPRINT",EDGE,{"derivedFrom":subQ6}),1.0]])]});}
            var Q4;
            {var subQ1=sQuery(id+"F0.wireOp",EDGE,"E3.1.0.1");var subQ2=makeQuery(id+"F1.opExtrude","CAP_EDGE",EDGE,{"disambiguationData":[OSD([subQ1])],"isStart":true});Q4=makeQuery(id+"F4.imprint","IMPRINT",FACE,{"disambiguationData":[TD([[makeQuery(id+"F4.imprint","IMPRINT",EDGE,{"derivedFrom":subQ2}),1.0]])]});}
            var Q5;
            {var subQ1=sQuery(id+"F0.wireOp",EDGE,"E1");var subQ2=makeQuery(id+"F1.opExtrude","CAP_EDGE",EDGE,{"disambiguationData":[OSD([subQ1])],"isStart":true});Q5=makeQuery(id+"F4.imprint","IMPRINT",FACE,{"disambiguationData":[TD([[makeQuery(id+"F4.imprint","IMPRINT",EDGE,{"derivedFrom":subQ2}),1.0]])]});}
            var Q6;
            {var subQ6=sQuery(id+"F0.wireOp",EDGE,"E16");var subQ7=makeQuery(id+"F1.opExtrude","CAP_EDGE",EDGE,{"disambiguationData":[OSD([subQ6]),TDD([makeQuery(id+"F0.imprint","IMPRINT",EDGE,{"disambiguationData":[TD([[makeQuery(id+"F0.imprint","INTERSECT",VERTEX,{"derivedFrom":[sQuery(id+"F0.wireOp",EDGE,"E0.left"),subQ6]}),1.0]])],"derivedFrom":subQ6})])],"isStart":true});Q6=makeQuery(id+"F4.imprint","IMPRINT",FACE,{"disambiguationData":[TD([[makeQuery(id+"F4.imprint","IMPRINT",EDGE,{"derivedFrom":subQ7}),-1.0]])]});}
            var Q7;
            {var subQ0=sQuery(id+"F4.wireOp",EDGE,"E63.left");Q7=makeQuery(id+"F4.imprint","IMPRINT",FACE,{"disambiguationData":[TD([[makeQuery(id+"F4.imprint","IMPRINT",EDGE,{"derivedFrom":subQ0}),1.0]])]});}
            var Q8;
            {var subQ2=sQuery(id+"F0.wireOp",EDGE,"E33");var subQ6=sQuery(id+"F0.wireOp",EDGE,"E3.4.0.0");var subQ9=makeQuery(id+"F1.opExtrude","CAP_EDGE",EDGE,{"disambiguationData":[OSD([subQ2]),TDD([makeQuery(id+"F0.imprint","IMPRINT",EDGE,{"disambiguationData":[TD([[makeQuery(id+"F0.imprint","INTERSECT",VERTEX,{"derivedFrom":[subQ6,subQ2]}),-1.0]])],"derivedFrom":subQ2})])],"isStart":true});Q8=makeQuery(id+"F4.imprint","IMPRINT",FACE,{"disambiguationData":[TD([[makeQuery(id+"F4.imprint","IMPRINT",EDGE,{"derivedFrom":subQ9}),1.0]])]});}
            var Q9;
            {var subQ1=sQuery(id+"F0.wireOp",EDGE,"E21.trimOffspring");var subQ7=sQuery(id+"F0.wireOp",EDGE,"E33");var subQ8=makeQuery(id+"F1.opExtrude","CAP_EDGE",EDGE,{"disambiguationData":[OSD([subQ7]),TDD([makeQuery(id+"F0.imprint","IMPRINT",EDGE,{"disambiguationData":[TD([[makeQuery(id+"F0.imprint","INTERSECT",VERTEX,{"derivedFrom":[subQ1,subQ7]}),1.0]])],"derivedFrom":subQ7})])],"isStart":true});Q9=makeQuery(id+"F4.imprint","IMPRINT",FACE,{"disambiguationData":[TD([[makeQuery(id+"F4.imprint","IMPRINT",EDGE,{"derivedFrom":subQ8}),1.0]])]});}
            var Q10;
            {var subQ4=sQuery(id+"F0.wireOp",EDGE,"E28");var subQ5=sQuery(id+"F0.wireOp",EDGE,"E33");var subQ6=makeQuery(id+"F0.imprint","INTERSECT",VERTEX,{"derivedFrom":[subQ4,subQ5]});var subQ9=makeQuery(id+"F1.opExtrude","CAP_EDGE",EDGE,{"disambiguationData":[OSD([subQ5]),TDD([makeQuery(id+"F0.imprint","IMPRINT",EDGE,{"disambiguationData":[TD([[subQ6,-1.0]])],"derivedFrom":subQ5})])],"isStart":true});Q10=makeQuery(id+"F4.imprint","IMPRINT",FACE,{"disambiguationData":[TD([[makeQuery(id+"F4.imprint","IMPRINT",EDGE,{"derivedFrom":subQ9}),1.0]])]});}
            var Q11;
            {var subQ4=sQuery(id+"F0.wireOp",EDGE,"E3.1.0.0");var subQ7=sQuery(id+"F0.wireOp",EDGE,"E16");var subQ8=makeQuery(id+"F1.opExtrude","CAP_EDGE",EDGE,{"disambiguationData":[OSD([subQ7]),TDD([makeQuery(id+"F0.imprint","IMPRINT",EDGE,{"disambiguationData":[TD([[makeQuery(id+"F0.imprint","INTERSECT",VERTEX,{"derivedFrom":[subQ4,subQ7]}),1.0]])],"derivedFrom":subQ7})])],"isStart":true});Q11=makeQuery(id+"F4.imprint","IMPRINT",FACE,{"disambiguationData":[TD([[makeQuery(id+"F4.imprint","IMPRINT",EDGE,{"derivedFrom":subQ8}),-1.0]])]});}
            var Q12;
            {var subQ4=sQuery(id+"F0.wireOp",EDGE,"E2");var subQ7=sQuery(id+"F0.wireOp",EDGE,"E16");var subQ8=makeQuery(id+"F1.opExtrude","CAP_EDGE",EDGE,{"disambiguationData":[OSD([subQ7]),TDD([makeQuery(id+"F0.imprint","IMPRINT",EDGE,{"disambiguationData":[TD([[makeQuery(id+"F0.imprint","INTERSECT",VERTEX,{"derivedFrom":[subQ4,subQ7]}),1.0]])],"derivedFrom":subQ7})])],"isStart":true});Q12=makeQuery(id+"F4.imprint","IMPRINT",FACE,{"disambiguationData":[TD([[makeQuery(id+"F4.imprint","IMPRINT",EDGE,{"derivedFrom":subQ8}),-1.0]])]});}
            var Q13;
            Q13=makeQuery(id+"F4.imprint","IMPRINT",FACE,{"disambiguationData":[TD([[makeQuery(id+"F4.imprint","IMPRINT",EDGE,{"derivedFrom":sQuery(id+"F4.wireOp",EDGE,"E61.bottom")}),-1.0]])]});
            extrude(context, id + "F5", {"entities" : qUnion([Q0, Q1, Q2, Q3, Q4, Q5, Q6, Q7, Q8, Q9, Q10, Q11, Q12, Q13]), "operationType" : NewBodyOperationType.ADD, "depth" : 12 * mm, "offsetDistance" : 25 * mm});
        }
        {
            var Q0;
            {var subQ0=sQuery(id+"F0.wireOp",EDGE,"E0.bottom");var subQ1=makeQuery(id+"F0.imprint","INTERSECT",VERTEX,{"derivedFrom":[subQ0,sQuery(id+"F0.wireOp",EDGE,"E3.3.0.0")]});var subQ2=makeQuery(id+"F0.imprint","INTERSECT",VERTEX,{"derivedFrom":[subQ0,sQuery(id+"F0.wireOp",EDGE,"E2")]});Q0=makeQuery(id+"F3.boolean.opBoolean","MERGE",FACE,{"derivedFrom":[makeQuery(id+"F1.opExtrude","SWEPT_FACE",FACE,{"disambiguationData":[OSD([subQ0]),TDD([makeQuery(id+"F0.imprint","IMPRINT",EDGE,{"disambiguationData":[TD([[makeQuery(id+"F0.imprint","INTERSECT",VERTEX,{"derivedFrom":[subQ0,sQuery(id+"F0.wireOp",EDGE,"E1")]}),-1.0]])],"derivedFrom":subQ0}),makeQuery(id+"F0.imprint","IMPRINT",EDGE,{"disambiguationData":[TD([[subQ2,-1.0]])],"derivedFrom":subQ0})])]}),makeQuery(id+"F1.opExtrude","SWEPT_FACE",FACE,{"disambiguationData":[OSD([subQ0]),TDD([makeQuery(id+"F0.imprint","IMPRINT",EDGE,{"disambiguationData":[TD([[makeQuery(id+"F0.imprint","INTERSECT",VERTEX,{"derivedFrom":[subQ0,sQuery(id+"F0.wireOp",EDGE,"E3.1.0.0")]}),1.0]])],"derivedFrom":subQ0})])]}),makeQuery(id+"F1.opExtrude","SWEPT_FACE",FACE,{"disambiguationData":[OSD([subQ0]),TDD([makeQuery(id+"F0.imprint","IMPRINT",EDGE,{"disambiguationData":[TD([[makeQuery(id+"F0.imprint","INTERSECT",VERTEX,{"derivedFrom":[subQ0,sQuery(id+"F0.wireOp",EDGE,"E3.2.0.0")]}),1.0]])],"derivedFrom":subQ0})])]}),makeQuery(id+"F1.opExtrude","SWEPT_FACE",FACE,{"disambiguationData":[OSD([subQ0]),TDD([makeQuery(id+"F0.imprint","IMPRINT",EDGE,{"disambiguationData":[TD([[subQ1,1.0]])],"derivedFrom":subQ0}),makeQuery(id+"F0.imprint","IMPRINT",EDGE,{"disambiguationData":[TD([[subQ1,-1.0]])],"derivedFrom":subQ0})])]}),makeQuery(id+"F1.opExtrude","SWEPT_FACE",FACE,{"disambiguationData":[OSD([subQ0]),TDD([makeQuery(id+"F0.imprint","IMPRINT",EDGE,{"disambiguationData":[TD([[makeQuery(id+"F0.imprint","INTERSECT",VERTEX,{"derivedFrom":[subQ0,sQuery(id+"F0.wireOp",EDGE,"E3.4.0.0")]}),1.0]])],"derivedFrom":subQ0})])]}),makeQuery(id+"F1.opExtrude","SWEPT_FACE",FACE,{"disambiguationData":[OSD([subQ0]),TDD([makeQuery(id+"F0.imprint","IMPRINT",EDGE,{"disambiguationData":[TD([[makeQuery(id+"F0.imprint","INTERSECT",VERTEX,{"derivedFrom":[subQ0,sQuery(id+"F0.wireOp",EDGE,"E3.5.0.0")]}),1.0]])],"derivedFrom":subQ0})])]}),makeQuery(id+"F1.opExtrude","SWEPT_FACE",FACE,{"disambiguationData":[OSD([subQ0]),TDD([makeQuery(id+"F0.imprint","IMPRINT",EDGE,{"disambiguationData":[TD([[makeQuery(id+"F0.imprint","INTERSECT",VERTEX,{"derivedFrom":[subQ0,sQuery(id+"F0.wireOp",EDGE,"E3.6.0.0")]}),1.0]])],"derivedFrom":subQ0})])]}),makeQuery(id+"F1.opExtrude","SWEPT_FACE",FACE,{"disambiguationData":[OSD([subQ0]),TDD([makeQuery(id+"F0.imprint","IMPRINT",EDGE,{"disambiguationData":[TD([[makeQuery(id+"F0.imprint","INTERSECT",VERTEX,{"derivedFrom":[subQ0,sQuery(id+"F0.wireOp",EDGE,"E3.7.0.0")]}),1.0]])],"derivedFrom":subQ0})])]}),makeQuery(id+"F1.opExtrude","SWEPT_FACE",FACE,{"disambiguationData":[OSD([subQ0]),TDD([makeQuery(id+"F0.imprint","IMPRINT",EDGE,{"disambiguationData":[TD([[makeQuery(id+"F0.imprint","INTERSECT",VERTEX,{"derivedFrom":[subQ0,sQuery(id+"F0.wireOp",EDGE,"E3.8.0.0")]}),1.0]])],"derivedFrom":subQ0})])]}),makeQuery(id+"F1.opExtrude","SWEPT_FACE",FACE,{"disambiguationData":[OSD([subQ0]),TDD([makeQuery(id+"F0.imprint","IMPRINT",EDGE,{"disambiguationData":[TD([[makeQuery(id+"F0.imprint","INTERSECT",VERTEX,{"derivedFrom":[subQ0,sQuery(id+"F0.wireOp",EDGE,"E3.9.0.0")]}),1.0]])],"derivedFrom":subQ0})])]}),makeQuery(id+"F1.opExtrude","SWEPT_FACE",FACE,{"disambiguationData":[OSD([subQ0]),TDD([makeQuery(id+"F0.imprint","IMPRINT",EDGE,{"disambiguationData":[TD([[makeQuery(id+"F0.imprint","INTERSECT",VERTEX,{"derivedFrom":[subQ0,sQuery(id+"F0.wireOp",EDGE,"E3.10.0.0")]}),1.0]])],"derivedFrom":subQ0})])]}),makeQuery(id+"F1.opExtrude","SWEPT_FACE",FACE,{"disambiguationData":[OSD([subQ0]),TDD([makeQuery(id+"F0.imprint","IMPRINT",EDGE,{"disambiguationData":[TD([[makeQuery(id+"F0.imprint","INTERSECT",VERTEX,{"derivedFrom":[subQ0,sQuery(id+"F0.wireOp",EDGE,"E3.11.0.0")]}),1.0]])],"derivedFrom":subQ0})])]}),makeQuery(id+"F1.opExtrude","SWEPT_FACE",FACE,{"disambiguationData":[OSD([sQuery(id+"F0.wireOp",EDGE,"E4.bottom")])]}),makeQuery(id+"F3.opExtrude","SWEPT_FACE",FACE,{"disambiguationData":[OSD([sQuery(id+"F2.wireOp",EDGE,"E55.bottom")])]})]});}
            var sketch = newSketch(context, id + "F6", { "sketchPlane" : qUnion([Q0])});
            skLineSegment(sketch, "E66.bottom", {"start": v(0, 0) * mm, "end": v(412, 0) * mm});
            skLineSegment(sketch, "E66.top", {"start": v(0, -7812) * mm, "end": v(412, -7812) * mm});
            skLineSegment(sketch, "E66.left", {"start": v(0, 0) * mm, "end": v(0, -7812) * mm});
            skLineSegment(sketch, "E66.right", {"start": v(412, 0) * mm, "end": v(412, -7812) * mm});
            skSolve(sketch);
        }
        {
            var Q0;
            Q0 = qSketchRegion(id + "F6", true);
            extrude(context, id + "F7", {"entities" : qUnion([Q0]), "operationType" : NewBodyOperationType.ADD, "depth" : 12 * mm, "offsetDistance" : 25 * mm});
        }
        {
            var Q0;
            Q0=makeQuery(id+"F7.boolean.opBoolean","MERGE",FACE,{"derivedFrom":[makeQuery(id+"F3.opExtrude","SWEPT_FACE",FACE,{"disambiguationData":[OSD([sQuery(id+"F2.wireOp",EDGE,"E55.left")])]}),makeQuery(id+"F7.opExtrude","SWEPT_FACE",FACE,{"disambiguationData":[OSD([sQuery(id+"F6.wireOp",EDGE,"E66.bottom")])]})]});
            var sketch = newSketch(context, id + "F8", { "sketchPlane" : qUnion([Q0])});
            skLineSegment(sketch, "E67", {"start": v(400, 2900) * mm, "end": v(-119.4, 3337.79) * mm});
            skLineSegment(sketch, "E68", {"start": v(-119.4, 3337.79) * mm, "end": v(515.77, 3337.79) * mm});
            skLineSegment(sketch, "E69", {"start": v(515.77, 3337.79) * mm, "end": v(515.77, 2802.42) * mm});
            skLineSegment(sketch, "E70", {"start": v(400, 2900) * mm, "end": v(515.77, 2802.42) * mm});
            skLineSegment(sketch, "E71", {"start": v(0, 2802.42) * mm, "end": v(0, 3237.15) * mm});
            skLineSegment(sketch, "E72", {"start": v(-12, 2802.42) * mm, "end": v(-12, 3247.26) * mm});
            skSolve(sketch);
        }
        {
            var Q0;
            Q0 = qSketchRegion(id + "F8", true);
            extrude(context, id + "F9", {"entities" : qUnion([Q0]), "operationType" : NewBodyOperationType.REMOVE, "oppositeDirection" : true, "depth" : 7400 * mm});
        }
    });
